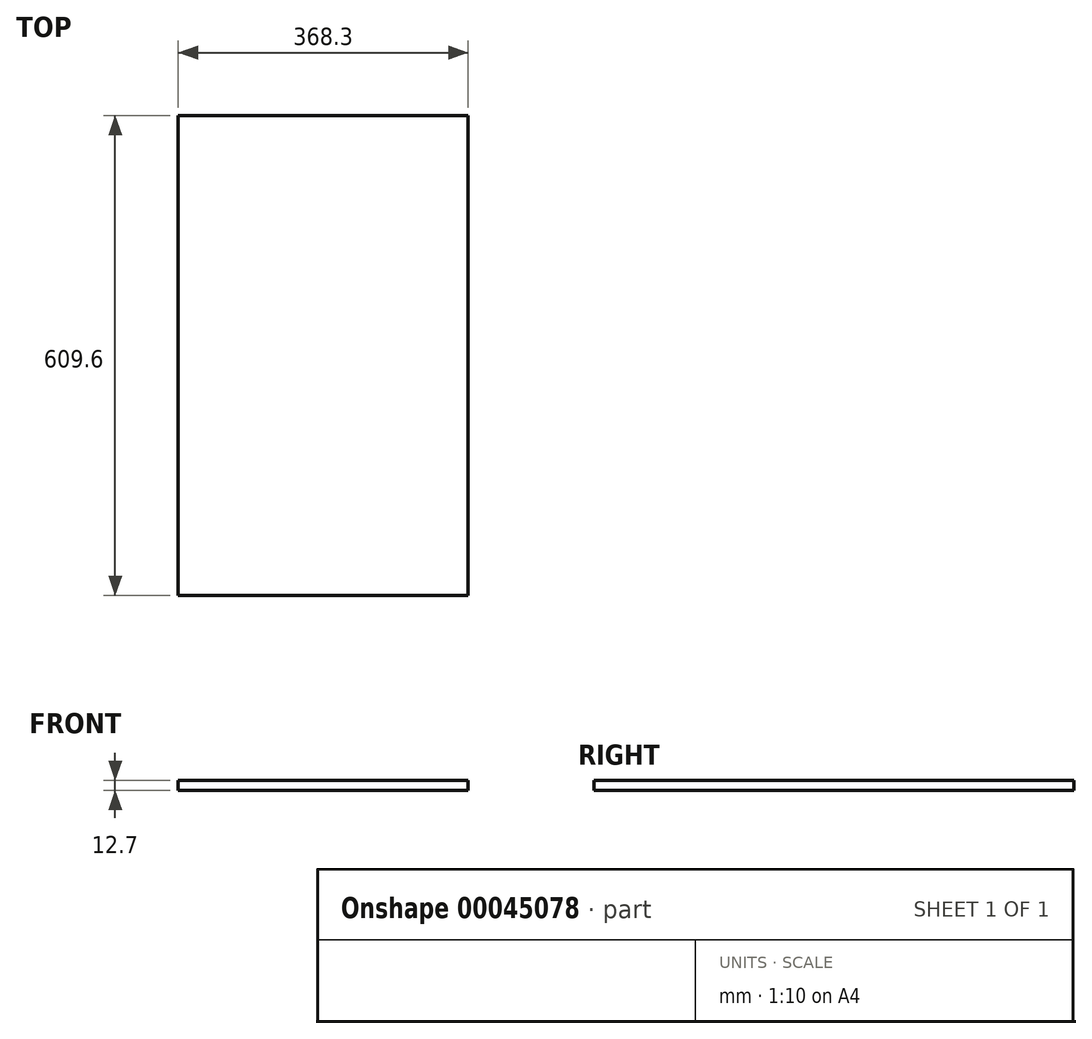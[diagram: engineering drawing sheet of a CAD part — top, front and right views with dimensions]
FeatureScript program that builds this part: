
annotation { "Feature Type Name" : "Feature", "Feature Type Description" : "" }
export const myFeature = defineFeature(function(context is Context, id is Id, definition is map)
    precondition{}
    {
        {
            var Q0;
            Q0=qCreatedBy(makeId("Top.planeOp"),FACE);
            var sketch = newSketch(context, id + "F0", { "sketchPlane" : qUnion([Q0])});
            skLineSegment(sketch, "E0.bottom", {"start": v(-31.38, 550.2) * mm, "end": v(336.92, 550.2) * mm});
            skLineSegment(sketch, "E0.top", {"start": v(-31.38, -59.4) * mm, "end": v(336.92, -59.4) * mm});
            skLineSegment(sketch, "E0.left", {"start": v(-31.38, 550.2) * mm, "end": v(-31.38, -59.4) * mm});
            skLineSegment(sketch, "E0.right", {"start": v(336.92, 550.2) * mm, "end": v(336.92, -59.4) * mm});
            skSolve(sketch);
        }
        {
            var Q0;
            Q0=makeQuery(id+"F0.imprint","IMPRINT",FACE,{"disambiguationData":[TD([[makeQuery(id+"F0.imprint","IMPRINT",EDGE,{"derivedFrom":sQuery(id+"F0.wireOp",EDGE,"E0.bottom")}),-1.0]])]});
            extrude(context, id + "F1", {"entities" : qUnion([Q0]), "depth" : 12.7 * mm});
        }
    });
